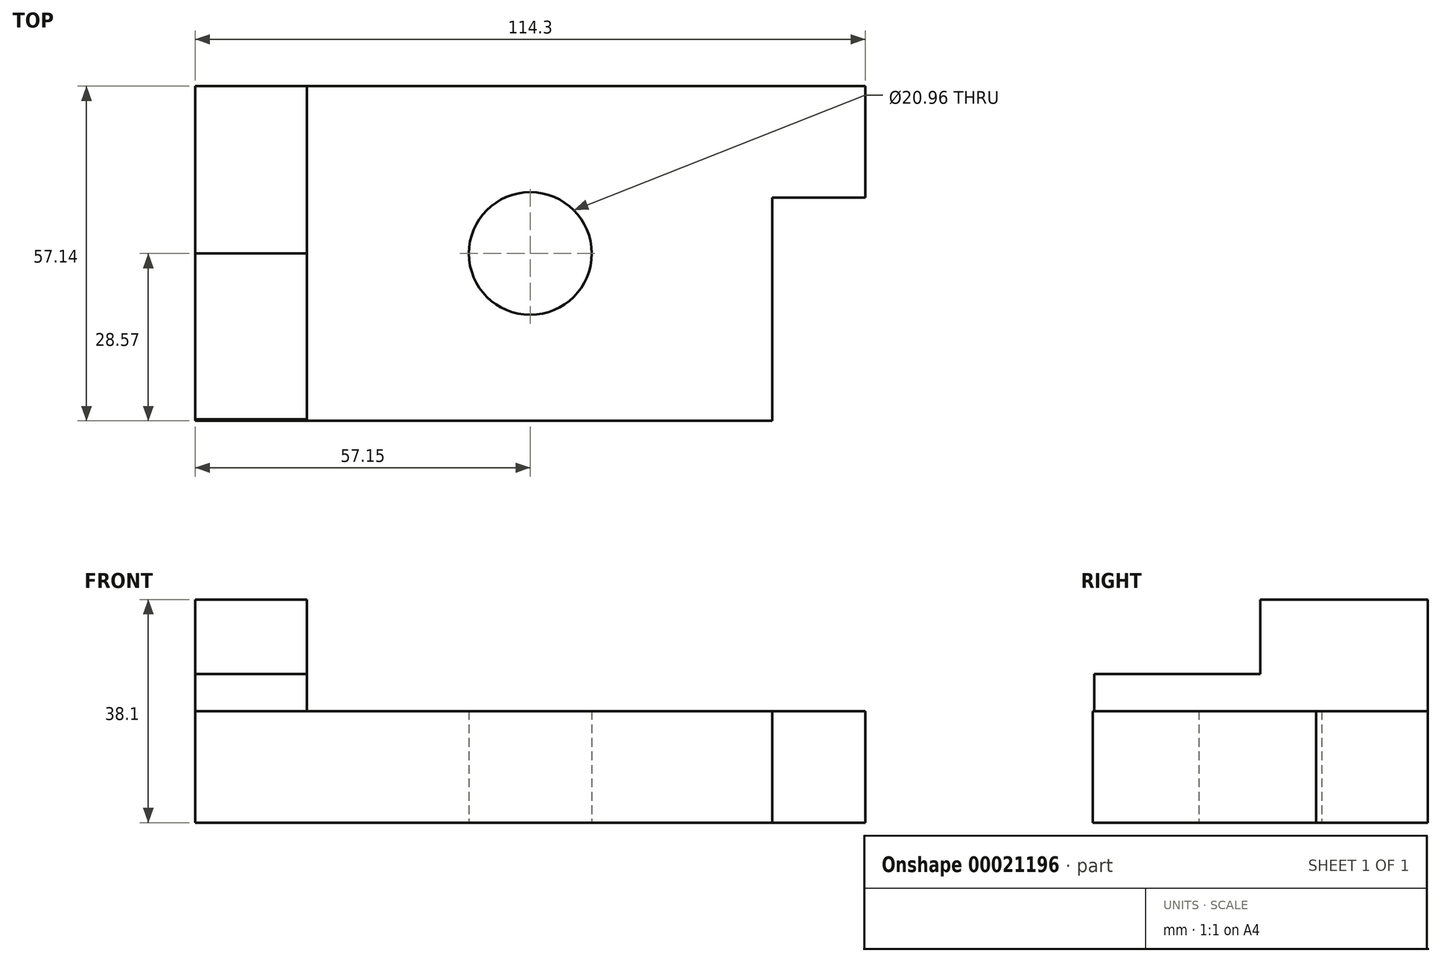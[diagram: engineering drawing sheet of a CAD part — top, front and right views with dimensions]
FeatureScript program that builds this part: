
annotation { "Feature Type Name" : "Feature", "Feature Type Description" : "" }
export const myFeature = defineFeature(function(context is Context, id is Id, definition is map)
    precondition{}
    {
        {
            var Q0;
            Q0=qCreatedBy(makeId("Top.planeOp"),FACE);
            var sketch = newSketch(context, id + "F0", { "sketchPlane" : qUnion([Q0])});
            skLineSegment(sketch, "E0.bottom", {"start": v(-57.15, 28.58) * mm, "end": v(57.15, 28.58) * mm});
            skLineSegment(sketch, "E0.top", {"start": v(-57.15, -28.57) * mm, "end": v(57.15, -28.57) * mm});
            skLineSegment(sketch, "E0.left", {"start": v(-57.15, 28.58) * mm, "end": v(-57.15, -28.57) * mm});
            skLineSegment(sketch, "E0.right", {"start": v(57.15, 28.58) * mm, "end": v(57.15, -28.57) * mm});
            skCircle(sketch, "E1", {"center": v(0, 0) * mm, "radius": 10.48 * mm});
            skLineSegment(sketch, "E2.bottom", {"start": v(41.28, 9.53) * mm, "end": v(57.15, 9.53) * mm});
            skLineSegment(sketch, "E2.top", {"start": v(41.28, -28.57) * mm, "end": v(57.15, -28.57) * mm});
            skLineSegment(sketch, "E2.left", {"start": v(41.28, 9.53) * mm, "end": v(41.28, -28.57) * mm});
            skLineSegment(sketch, "E2.right", {"start": v(57.15, 9.53) * mm, "end": v(57.15, -28.57) * mm});
            skSolve(sketch);
        }
        {
            var Q0;
            Q0=makeQuery(id+"F0.imprint","IMPRINT",FACE,{"disambiguationData":[TD([[makeQuery(id+"F0.imprint","IMPRINT",EDGE,{"derivedFrom":sQuery(id+"F0.wireOp",EDGE,"E0.bottom")}),-1.0]])]});
            extrude(context, id + "F1", {"entities" : qUnion([Q0]), "depth" : 19.05 * mm});
        }
        {
            var Q0;
            Q0=makeQuery(id+"F1.opExtrude","SWEPT_FACE",FACE,{"disambiguationData":[OSD([sQuery(id+"F0.wireOp",EDGE,"E0.left")])]});
            var sketch = newSketch(context, id + "F2", { "sketchPlane" : qUnion([Q0])});
            skLineSegment(sketch, "E3.bottom", {"start": v(-28.58, 19.05) * mm, "end": v(0, 19.05) * mm});
            skLineSegment(sketch, "E3.top", {"start": v(-28.58, 38.1) * mm, "end": v(0, 38.1) * mm});
            skLineSegment(sketch, "E3.left", {"start": v(-28.58, 19.05) * mm, "end": v(-28.58, 38.1) * mm});
            skLineSegment(sketch, "E3.right", {"start": v(0, 19.05) * mm, "end": v(0, 38.1) * mm});
            skLineSegment(sketch, "E4.bottom", {"start": v(0, 19.05) * mm, "end": v(28.3, 19.05) * mm});
            skLineSegment(sketch, "E4.top", {"start": v(0, 25.4) * mm, "end": v(28.3, 25.4) * mm});
            skLineSegment(sketch, "E4.left", {"start": v(0, 19.05) * mm, "end": v(0, 25.4) * mm});
            skLineSegment(sketch, "E4.right", {"start": v(28.3, 19.05) * mm, "end": v(28.3, 25.4) * mm});
            skSolve(sketch);
        }
        {
            var Q0;
            Q0=makeQuery(id+"F2.imprint","IMPRINT",FACE,{"disambiguationData":[TD([[makeQuery(id+"F2.imprint","IMPRINT",EDGE,{"derivedFrom":sQuery(id+"F2.wireOp",EDGE,"E3.bottom")}),1.0]])]});
            var Q1;
            Q1=makeQuery(id+"F2.imprint","IMPRINT",FACE,{"disambiguationData":[TD([[makeQuery(id+"F2.imprint","IMPRINT",EDGE,{"derivedFrom":sQuery(id+"F2.wireOp",EDGE,"E4.bottom")}),1.0]])]});
            extrude(context, id + "F3", {"entities" : qUnion([Q0, Q1]), "oppositeDirection" : true, "depth" : 19.05 * mm});
        }
    });
